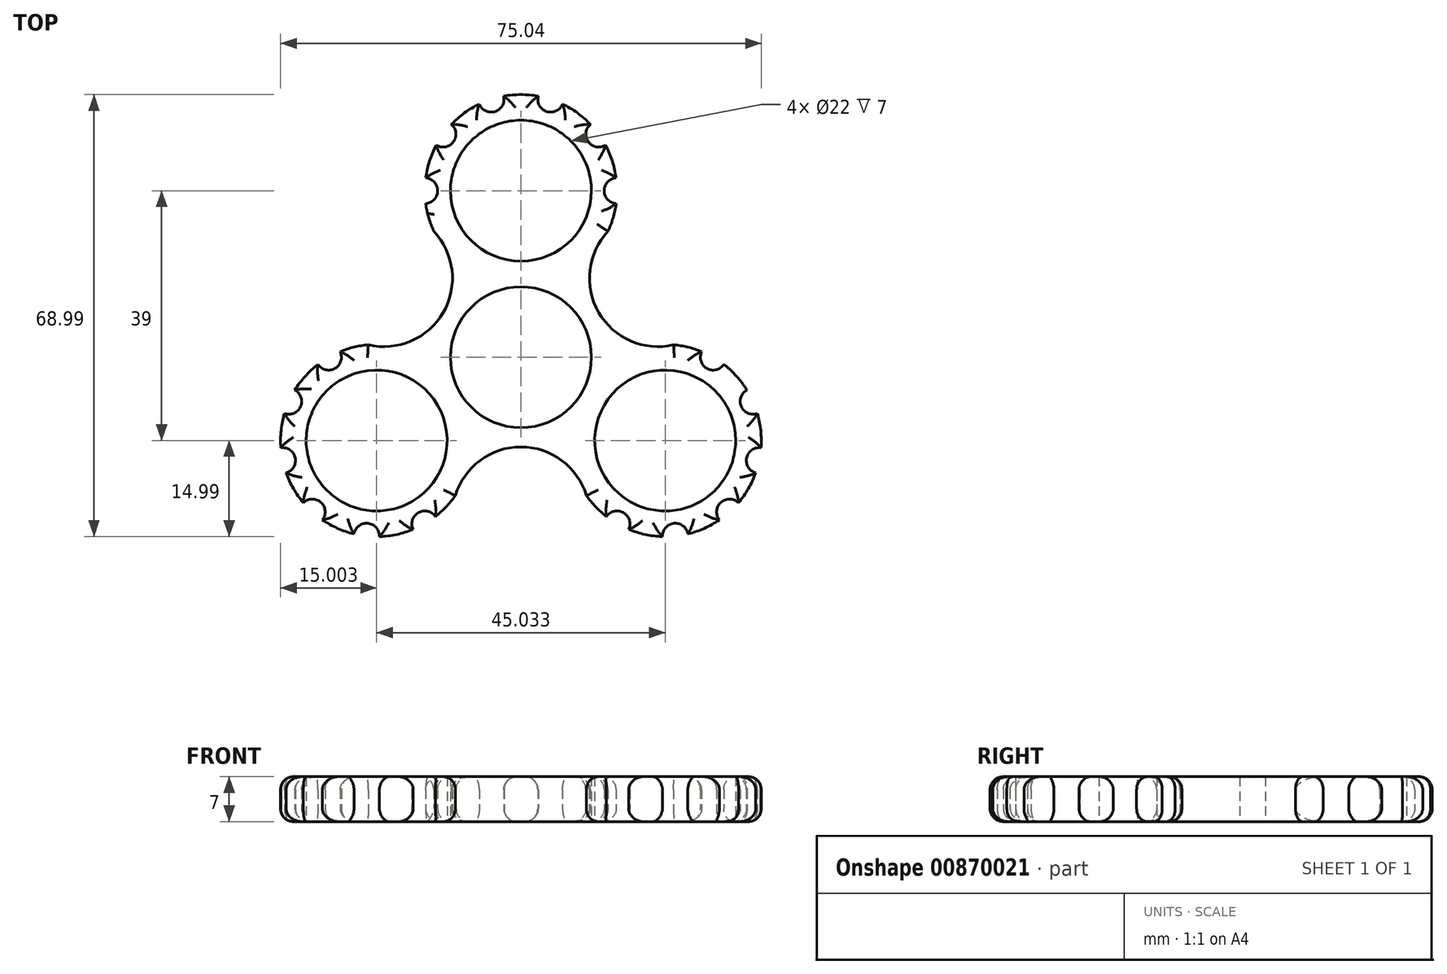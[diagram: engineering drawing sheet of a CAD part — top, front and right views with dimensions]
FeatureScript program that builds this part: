
annotation { "Feature Type Name" : "Feature", "Feature Type Description" : "" }
export const myFeature = defineFeature(function(context is Context, id is Id, definition is map)
    precondition{}
    {
        {
            var Q0;
            Q0=qCreatedBy(makeId("Top.planeOp"),FACE);
            var sketch = newSketch(context, id + "F0", { "sketchPlane" : qUnion([Q0])});
            skCircle(sketch, "E0", {"center": v(0, 0) * mm, "radius": 11 * mm});
            skCircle(sketch, "E1.0", {"center": v(0, 0) * mm, "radius": 14 * mm});
            skLineSegment(sketch, "E2", {"start": v(0, 0) * mm, "end": v(0, 26) * mm});
            skCircle(sketch, "E3", {"center": v(0, 26) * mm, "radius": 11 * mm});
            skCircle(sketch, "E4.0", {"center": v(0, 26) * mm, "radius": 15 * mm});
            skCircle(sketch, "E5", {"center": v(-15, 26) * mm, "radius": 2 * mm});
            skCircle(sketch, "E6.1.0", {"center": v(-12.14, 34.82) * mm, "radius": 2 * mm});
            skCircle(sketch, "E6.2.0", {"center": v(-4.64, 40.27) * mm, "radius": 2 * mm});
            skLineSegment(sketch, "E6.anchor1", {"start": v(0, 26) * mm, "end": v(-15, 26) * mm, "construction": true});
            skLineSegment(sketch, "E6.anchor2", {"start": v(0, 26) * mm, "end": v(15, 26) * mm, "construction": true});
            skCircle(sketch, "E7.1.3.0", {"center": v(4.64, 40.27) * mm, "radius": 2 * mm});
            skCircle(sketch, "E7.1.4.0", {"center": v(12.14, 34.82) * mm, "radius": 2 * mm});
            skPoint(sketch, "E8", {"position": v(-14.87, 24) * mm});
            skLineSegment(sketch, "E9", {"start": v(0, 0) * mm, "end": v(12.12, 7) * mm});
            skPoint(sketch, "E10.MirrorP", {"position": v(14.87, 24) * mm});
            skCircle(sketch, "E11.1.5.0", {"center": v(15, 26) * mm, "radius": 2 * mm});
            skLineSegment(sketch, "E12", {"start": v(0, 26) * mm, "end": v(13.6, 19.66) * mm});
            skCircle(sketch, "E13.1.0", {"center": v(-22.52, -13) * mm, "radius": 15 * mm});
            skCircle(sketch, "E13.1.1", {"center": v(-22.52, -13) * mm, "radius": 11 * mm});
            skCircle(sketch, "E13.1.2", {"center": v(-15.02, -26) * mm, "radius": 2 * mm});
            skCircle(sketch, "E13.1.3", {"center": v(-24.08, -27.92) * mm, "radius": 2 * mm});
            skCircle(sketch, "E13.1.4", {"center": v(-32.55, -24.15) * mm, "radius": 2 * mm});
            skCircle(sketch, "E13.1.5", {"center": v(-37.19, -16.12) * mm, "radius": 2 * mm});
            skCircle(sketch, "E13.1.6", {"center": v(-36.22, -6.9) * mm, "radius": 2 * mm});
            skCircle(sketch, "E13.1.7", {"center": v(-30.02, 0) * mm, "radius": 2 * mm});
            skCircle(sketch, "E13.2.0", {"center": v(22.52, -13) * mm, "radius": 15 * mm});
            skCircle(sketch, "E13.2.1", {"center": v(22.52, -13) * mm, "radius": 11 * mm});
            skCircle(sketch, "E13.2.2", {"center": v(30.02, 0) * mm, "radius": 2 * mm});
            skCircle(sketch, "E13.2.3", {"center": v(36.22, -6.9) * mm, "radius": 2 * mm});
            skCircle(sketch, "E13.2.4", {"center": v(37.19, -16.12) * mm, "radius": 2 * mm});
            skCircle(sketch, "E13.2.5", {"center": v(32.55, -24.15) * mm, "radius": 2 * mm});
            skCircle(sketch, "E13.2.6", {"center": v(24.08, -27.92) * mm, "radius": 2 * mm});
            skCircle(sketch, "E13.2.7", {"center": v(15.02, -26) * mm, "radius": 2 * mm});
            skLineSegment(sketch, "E14.MirrorCS", {"start": v(22.52, -13) * mm, "end": v(23.82, 1.94) * mm});
            skArc(sketch, "E15", {"start": v(13.6, 19.66) * mm, "mid": v(12.12, 7) * mm, "end": v(23.82, 1.94) * mm});
            skArc(sketch, "E16.1.0", {"start": v(-23.82, 1.94) * mm, "mid": v(-12.12, 7) * mm, "end": v(-13.6, 19.66) * mm});
            skArc(sketch, "E16.2.0", {"start": v(10.23, -21.6) * mm, "mid": v(0, -14) * mm, "end": v(-10.23, -21.6) * mm});
            skSolve(sketch);
        }
        {
            var Q0;
            {var subQ3=sQuery(id+"F0.wireOp",EDGE,"E1.0");var subQ18=sQuery(id+"F0.wireOp",EDGE,"E2");var subQ19=makeQuery(id+"F0.imprint","INTERSECT",VERTEX,{"derivedFrom":[subQ3,subQ18]});Q0=makeQuery(id+"F0.imprint","IMPRINT",FACE,{"disambiguationData":[TD([[makeQuery(id+"F0.imprint","IMPRINT",EDGE,{"disambiguationData":[TD([[subQ19,-1.0]])],"derivedFrom":subQ3}),-1.0]])]});}
            var Q1;
            {var subQ5=sQuery(id+"F0.wireOp",EDGE,"E1.0");var subQ7=sQuery(id+"F0.wireOp",EDGE,"E4.0");var subQ8=makeQuery(id+"F0.imprint","INTERSECT",VERTEX,{"disambiguationData":[OD(0.0)],"derivedFrom":[subQ5,subQ7]});Q1=makeQuery(id+"F0.imprint","IMPRINT",FACE,{"disambiguationData":[TD([[makeQuery(id+"F0.imprint","IMPRINT",EDGE,{"disambiguationData":[TD([[subQ8,-1.0]])],"derivedFrom":subQ5}),-1.0]])]});}
            var Q2;
            {var subQ0=sQuery(id+"F0.wireOp",EDGE,"E4.0");var subQ1=sQuery(id+"F0.wireOp",EDGE,"E1.0");var subQ2=makeQuery(id+"F0.imprint","INTERSECT",VERTEX,{"disambiguationData":[OD(0.0)],"derivedFrom":[subQ1,subQ0]});Q2=makeQuery(id+"F0.imprint","IMPRINT",FACE,{"disambiguationData":[TD([[makeQuery(id+"F0.imprint","IMPRINT",EDGE,{"disambiguationData":[TD([[subQ2,-1.0]])],"derivedFrom":subQ1}),1.0]])]});}
            var Q3;
            {var subQ0=sQuery(id+"F0.wireOp",EDGE,"E2");var subQ1=sQuery(id+"F0.wireOp",EDGE,"E1.0");var subQ2=makeQuery(id+"F0.imprint","INTERSECT",VERTEX,{"derivedFrom":[subQ1,subQ0]});Q3=makeQuery(id+"F0.imprint","IMPRINT",FACE,{"disambiguationData":[TD([[makeQuery(id+"F0.imprint","IMPRINT",EDGE,{"disambiguationData":[TD([[subQ2,-1.0]])],"derivedFrom":subQ1}),1.0]])]});}
            var Q4;
            {var subQ0=sQuery(id+"F0.wireOp",EDGE,"E16.1.0");var subQ1=sQuery(id+"F0.wireOp",EDGE,"E1.0");var subQ2=makeQuery(id+"F0.imprint","INTERSECT",VERTEX,{"derivedFrom":[subQ1,subQ0]});Q4=makeQuery(id+"F0.imprint","IMPRINT",FACE,{"disambiguationData":[TD([[makeQuery(id+"F0.imprint","IMPRINT",EDGE,{"disambiguationData":[TD([[subQ2,1.0]])],"derivedFrom":subQ1}),-1.0]])]});}
            var Q5;
            {var subQ1=sQuery(id+"F0.wireOp",EDGE,"E1.0");var subQ5=makeQuery(id+"F0.imprint","INTERSECT",VERTEX,{"derivedFrom":[subQ1,sQuery(id+"F0.wireOp",EDGE,"E16.1.0")]});Q5=makeQuery(id+"F0.imprint","IMPRINT",FACE,{"disambiguationData":[TD([[makeQuery(id+"F0.imprint","IMPRINT",EDGE,{"disambiguationData":[TD([[subQ5,1.0]])],"derivedFrom":subQ1}),1.0]])]});}
            var Q6;
            {var subQ0=sQuery(id+"F0.wireOp",EDGE,"E16.1.0");var subQ1=sQuery(id+"F0.wireOp",EDGE,"E1.0");var subQ2=makeQuery(id+"F0.imprint","INTERSECT",VERTEX,{"derivedFrom":[subQ1,subQ0]});Q6=makeQuery(id+"F0.imprint","IMPRINT",FACE,{"disambiguationData":[TD([[makeQuery(id+"F0.imprint","IMPRINT",EDGE,{"disambiguationData":[TD([[subQ2,-1.0]])],"derivedFrom":subQ1}),-1.0]])]});}
            var Q7;
            Q7=makeQuery(id+"F0.imprint","IMPRINT",FACE,{"disambiguationData":[TD([[makeQuery(id+"F0.imprint","IMPRINT",EDGE,{"derivedFrom":sQuery(id+"F0.wireOp",EDGE,"E13.1.1")}),-1.0]])]});
            var Q8;
            {var subQ0=sQuery(id+"F0.wireOp",EDGE,"E13.1.0");var subQ1=sQuery(id+"F0.wireOp",EDGE,"E1.0");var subQ2=makeQuery(id+"F0.imprint","INTERSECT",VERTEX,{"disambiguationData":[OD(0.0)],"derivedFrom":[subQ1,subQ0]});Q8=makeQuery(id+"F0.imprint","IMPRINT",FACE,{"disambiguationData":[TD([[makeQuery(id+"F0.imprint","IMPRINT",EDGE,{"disambiguationData":[TD([[subQ2,-1.0]])],"derivedFrom":subQ1}),1.0]])]});}
            var Q9;
            {var subQ0=sQuery(id+"F0.wireOp",EDGE,"E13.1.0");var subQ1=sQuery(id+"F0.wireOp",EDGE,"E0");var subQ2=makeQuery(id+"F0.imprint","INTERSECT",VERTEX,{"derivedFrom":[subQ1,subQ0]});Q9=makeQuery(id+"F0.imprint","IMPRINT",FACE,{"disambiguationData":[TD([[makeQuery(id+"F0.imprint","IMPRINT",EDGE,{"disambiguationData":[TD([[subQ2,-1.0]])],"derivedFrom":subQ1}),-1.0]])]});}
            var Q10;
            {var subQ0=sQuery(id+"F0.wireOp",EDGE,"E16.2.0");var subQ1=sQuery(id+"F0.wireOp",EDGE,"E1.0");var subQ2=makeQuery(id+"F0.imprint","INTERSECT",VERTEX,{"derivedFrom":[subQ1,subQ0]});Q10=makeQuery(id+"F0.imprint","IMPRINT",FACE,{"disambiguationData":[TD([[makeQuery(id+"F0.imprint","IMPRINT",EDGE,{"disambiguationData":[TD([[subQ2,1.0]])],"derivedFrom":subQ1}),-1.0]])]});}
            var Q11;
            {var subQ0=sQuery(id+"F0.wireOp",EDGE,"E16.2.0");var subQ1=sQuery(id+"F0.wireOp",EDGE,"E1.0");var subQ2=makeQuery(id+"F0.imprint","INTERSECT",VERTEX,{"derivedFrom":[subQ1,subQ0]});Q11=makeQuery(id+"F0.imprint","IMPRINT",FACE,{"disambiguationData":[TD([[makeQuery(id+"F0.imprint","IMPRINT",EDGE,{"disambiguationData":[TD([[subQ2,-1.0]])],"derivedFrom":subQ1}),-1.0]])]});}
            var Q12;
            Q12=makeQuery(id+"F0.imprint","IMPRINT",FACE,{"disambiguationData":[TD([[makeQuery(id+"F0.imprint","IMPRINT",EDGE,{"derivedFrom":sQuery(id+"F0.wireOp",EDGE,"E13.2.1")}),-1.0]])]});
            var Q13;
            {var subQ0=sQuery(id+"F0.wireOp",EDGE,"E13.2.0");var subQ1=sQuery(id+"F0.wireOp",EDGE,"E1.0");var subQ2=makeQuery(id+"F0.imprint","INTERSECT",VERTEX,{"disambiguationData":[OD(0.0)],"derivedFrom":[subQ1,subQ0]});Q13=makeQuery(id+"F0.imprint","IMPRINT",FACE,{"disambiguationData":[TD([[makeQuery(id+"F0.imprint","IMPRINT",EDGE,{"disambiguationData":[TD([[subQ2,-1.0]])],"derivedFrom":subQ1}),1.0]])]});}
            var Q14;
            {var subQ0=sQuery(id+"F0.wireOp",EDGE,"E15");var subQ3=sQuery(id+"F0.wireOp",EDGE,"E13.2.0");var subQ5=makeQuery(id+"F0.imprint","INTERSECT",VERTEX,{"disambiguationData":[OD(1.0)],"derivedFrom":[subQ3,subQ0]});Q14=makeQuery(id+"F0.imprint","IMPRINT",FACE,{"disambiguationData":[TD([[makeQuery(id+"F0.imprint","IMPRINT",EDGE,{"disambiguationData":[TD([[subQ5,-1.0]])],"derivedFrom":subQ3}),-1.0]])]});}
            var Q15;
            {var subQ0=sQuery(id+"F0.wireOp",EDGE,"E9");var subQ1=sQuery(id+"F0.wireOp",EDGE,"E0");var subQ2=makeQuery(id+"F0.imprint","INTERSECT",VERTEX,{"derivedFrom":[subQ1,subQ0]});Q15=makeQuery(id+"F0.imprint","IMPRINT",FACE,{"disambiguationData":[TD([[makeQuery(id+"F0.imprint","IMPRINT",EDGE,{"disambiguationData":[TD([[subQ2,1.0]])],"derivedFrom":subQ1}),-1.0]])]});}
            var Q16;
            {var subQ0=sQuery(id+"F0.wireOp",EDGE,"E15");var subQ3=sQuery(id+"F0.wireOp",EDGE,"E4.0");var subQ5=makeQuery(id+"F0.imprint","INTERSECT",VERTEX,{"derivedFrom":[subQ3,subQ0]});Q16=makeQuery(id+"F0.imprint","IMPRINT",FACE,{"disambiguationData":[TD([[makeQuery(id+"F0.imprint","IMPRINT",EDGE,{"disambiguationData":[TD([[subQ5,1.0]])],"derivedFrom":subQ3}),-1.0]])]});}
            var Q17;
            {var subQ0=sQuery(id+"F0.wireOp",EDGE,"E9");var subQ1=sQuery(id+"F0.wireOp",EDGE,"E0");var subQ2=makeQuery(id+"F0.imprint","INTERSECT",VERTEX,{"derivedFrom":[subQ1,subQ0]});Q17=makeQuery(id+"F0.imprint","IMPRINT",FACE,{"disambiguationData":[TD([[makeQuery(id+"F0.imprint","IMPRINT",EDGE,{"disambiguationData":[TD([[subQ2,-1.0]])],"derivedFrom":subQ1}),-1.0]])]});}
            extrude(context, id + "F1", {"entities" : qUnion([Q0, Q1, Q2, Q3, Q4, Q5, Q6, Q7, Q8, Q9, Q10, Q11, Q12, Q13, Q14, Q15, Q16, Q17]), "depth" : 7 * mm, "offsetDistance" : 25 * mm});
        }
        {
            var Q0;
            Q0=makeQuery(id+"F1.opExtrude","CAP_EDGE",EDGE,{"disambiguationData":[OSD([sQuery(id+"F0.wireOp",EDGE,"E15")])],"isStart":false});
            var Q1;
            {var subQ0=sQuery(id+"F0.wireOp",EDGE,"E13.2.0");Q1=makeQuery(id+"F1.opExtrude","CAP_EDGE",EDGE,{"disambiguationData":[OSD([subQ0]),TDD([makeQuery(id+"F0.imprint","IMPRINT",EDGE,{"disambiguationData":[TD([[makeQuery(id+"F0.imprint","INTERSECT",VERTEX,{"disambiguationData":[OD(0.0)],"derivedFrom":[subQ0,sQuery(id+"F0.wireOp",EDGE,"E15")]}),1.0]])],"derivedFrom":subQ0})])],"isStart":false});}
            var Q2;
            Q2=makeQuery(id+"F1.opExtrude","CAP_EDGE",EDGE,{"disambiguationData":[OSD([sQuery(id+"F0.wireOp",EDGE,"E13.2.2")])],"isStart":false});
            var Q3;
            {var subQ0=sQuery(id+"F0.wireOp",EDGE,"E13.2.0");Q3=makeQuery(id+"F1.opExtrude","CAP_EDGE",EDGE,{"disambiguationData":[OSD([subQ0]),TDD([makeQuery(id+"F0.imprint","IMPRINT",EDGE,{"disambiguationData":[TD([[makeQuery(id+"F0.imprint","INTERSECT",VERTEX,{"disambiguationData":[OD(1.0)],"derivedFrom":[subQ0,sQuery(id+"F0.wireOp",EDGE,"E13.2.3")]}),-1.0]])],"derivedFrom":subQ0})])],"isStart":false});}
            var Q4;
            Q4=makeQuery(id+"F1.opExtrude","CAP_EDGE",EDGE,{"disambiguationData":[OSD([sQuery(id+"F0.wireOp",EDGE,"E13.2.3")])],"isStart":false});
            var Q5;
            {var subQ0=sQuery(id+"F0.wireOp",EDGE,"E13.2.0");Q5=makeQuery(id+"F1.opExtrude","CAP_EDGE",EDGE,{"disambiguationData":[OSD([subQ0]),TDD([makeQuery(id+"F0.imprint","IMPRINT",EDGE,{"disambiguationData":[TD([[makeQuery(id+"F0.imprint","INTERSECT",VERTEX,{"disambiguationData":[OD(1.0)],"derivedFrom":[subQ0,sQuery(id+"F0.wireOp",EDGE,"E13.2.4")]}),-1.0]])],"derivedFrom":subQ0})])],"isStart":false});}
            var Q6;
            Q6=makeQuery(id+"F1.opExtrude","CAP_EDGE",EDGE,{"disambiguationData":[OSD([sQuery(id+"F0.wireOp",EDGE,"E13.2.4")])],"isStart":false});
            var Q7;
            {var subQ0=sQuery(id+"F0.wireOp",EDGE,"E13.2.0");Q7=makeQuery(id+"F1.opExtrude","CAP_EDGE",EDGE,{"disambiguationData":[OSD([subQ0]),TDD([makeQuery(id+"F0.imprint","IMPRINT",EDGE,{"disambiguationData":[TD([[makeQuery(id+"F0.imprint","INTERSECT",VERTEX,{"disambiguationData":[OD(1.0)],"derivedFrom":[subQ0,sQuery(id+"F0.wireOp",EDGE,"E13.2.5")]}),-1.0]])],"derivedFrom":subQ0})])],"isStart":false});}
            var Q8;
            Q8=makeQuery(id+"F1.opExtrude","CAP_EDGE",EDGE,{"disambiguationData":[OSD([sQuery(id+"F0.wireOp",EDGE,"E13.2.5")])],"isStart":false});
            var Q9;
            {var subQ0=sQuery(id+"F0.wireOp",EDGE,"E13.2.0");Q9=makeQuery(id+"F1.opExtrude","CAP_EDGE",EDGE,{"disambiguationData":[OSD([subQ0]),TDD([makeQuery(id+"F0.imprint","IMPRINT",EDGE,{"disambiguationData":[TD([[makeQuery(id+"F0.imprint","INTERSECT",VERTEX,{"disambiguationData":[OD(1.0)],"derivedFrom":[subQ0,sQuery(id+"F0.wireOp",EDGE,"E13.2.6")]}),-1.0]])],"derivedFrom":subQ0})])],"isStart":false});}
            var Q10;
            Q10=makeQuery(id+"F1.opExtrude","CAP_EDGE",EDGE,{"disambiguationData":[OSD([sQuery(id+"F0.wireOp",EDGE,"E13.2.6")])],"isStart":false});
            var Q11;
            {var subQ0=sQuery(id+"F0.wireOp",EDGE,"E13.2.0");Q11=makeQuery(id+"F1.opExtrude","CAP_EDGE",EDGE,{"disambiguationData":[OSD([subQ0]),TDD([makeQuery(id+"F0.imprint","IMPRINT",EDGE,{"disambiguationData":[TD([[makeQuery(id+"F0.imprint","INTERSECT",VERTEX,{"disambiguationData":[OD(0.0)],"derivedFrom":[subQ0,sQuery(id+"F0.wireOp",EDGE,"E13.2.6")]}),1.0]])],"derivedFrom":subQ0})])],"isStart":false});}
            var Q12;
            Q12=makeQuery(id+"F1.opExtrude","CAP_EDGE",EDGE,{"disambiguationData":[OSD([sQuery(id+"F0.wireOp",EDGE,"E13.2.7")])],"isStart":false});
            var Q13;
            {var subQ0=sQuery(id+"F0.wireOp",EDGE,"E13.2.0");Q13=makeQuery(id+"F1.opExtrude","CAP_EDGE",EDGE,{"disambiguationData":[OSD([subQ0]),TDD([makeQuery(id+"F0.imprint","IMPRINT",EDGE,{"disambiguationData":[TD([[makeQuery(id+"F0.imprint","INTERSECT",VERTEX,{"disambiguationData":[OD(0.0)],"derivedFrom":[subQ0,sQuery(id+"F0.wireOp",EDGE,"E16.2.0")]}),-1.0]])],"derivedFrom":subQ0})])],"isStart":false});}
            var Q14;
            Q14=makeQuery(id+"F1.opExtrude","CAP_EDGE",EDGE,{"disambiguationData":[OSD([sQuery(id+"F0.wireOp",EDGE,"E16.2.0")])],"isStart":false});
            var Q15;
            {var subQ0=sQuery(id+"F0.wireOp",EDGE,"E13.1.0");Q15=makeQuery(id+"F1.opExtrude","CAP_EDGE",EDGE,{"disambiguationData":[OSD([subQ0]),TDD([makeQuery(id+"F0.imprint","IMPRINT",EDGE,{"disambiguationData":[TD([[makeQuery(id+"F0.imprint","INTERSECT",VERTEX,{"disambiguationData":[OD(0.0)],"derivedFrom":[subQ0,sQuery(id+"F0.wireOp",EDGE,"E16.2.0")]}),1.0]])],"derivedFrom":subQ0})])],"isStart":false});}
            var Q16;
            Q16=makeQuery(id+"F1.opExtrude","CAP_EDGE",EDGE,{"disambiguationData":[OSD([sQuery(id+"F0.wireOp",EDGE,"E13.1.2")])],"isStart":false});
            var Q17;
            {var subQ0=sQuery(id+"F0.wireOp",EDGE,"E13.1.0");Q17=makeQuery(id+"F1.opExtrude","CAP_EDGE",EDGE,{"disambiguationData":[OSD([subQ0]),TDD([makeQuery(id+"F0.imprint","IMPRINT",EDGE,{"disambiguationData":[TD([[makeQuery(id+"F0.imprint","INTERSECT",VERTEX,{"disambiguationData":[OD(1.0)],"derivedFrom":[subQ0,sQuery(id+"F0.wireOp",EDGE,"E13.1.3")]}),-1.0]])],"derivedFrom":subQ0})])],"isStart":false});}
            var Q18;
            Q18=makeQuery(id+"F1.opExtrude","CAP_EDGE",EDGE,{"disambiguationData":[OSD([sQuery(id+"F0.wireOp",EDGE,"E13.1.3")])],"isStart":false});
            var Q19;
            {var subQ0=sQuery(id+"F0.wireOp",EDGE,"E13.1.0");Q19=makeQuery(id+"F1.opExtrude","CAP_EDGE",EDGE,{"disambiguationData":[OSD([subQ0]),TDD([makeQuery(id+"F0.imprint","IMPRINT",EDGE,{"disambiguationData":[TD([[makeQuery(id+"F0.imprint","INTERSECT",VERTEX,{"disambiguationData":[OD(1.0)],"derivedFrom":[subQ0,sQuery(id+"F0.wireOp",EDGE,"E13.1.4")]}),-1.0]])],"derivedFrom":subQ0})])],"isStart":false});}
            var Q20;
            Q20=makeQuery(id+"F1.opExtrude","CAP_EDGE",EDGE,{"disambiguationData":[OSD([sQuery(id+"F0.wireOp",EDGE,"E13.1.4")])],"isStart":false});
            var Q21;
            {var subQ0=sQuery(id+"F0.wireOp",EDGE,"E13.1.0");Q21=makeQuery(id+"F1.opExtrude","CAP_EDGE",EDGE,{"disambiguationData":[OSD([subQ0]),TDD([makeQuery(id+"F0.imprint","IMPRINT",EDGE,{"disambiguationData":[TD([[makeQuery(id+"F0.imprint","INTERSECT",VERTEX,{"disambiguationData":[OD(1.0)],"derivedFrom":[subQ0,sQuery(id+"F0.wireOp",EDGE,"E13.1.5")]}),-1.0]])],"derivedFrom":subQ0})])],"isStart":false});}
            var Q22;
            Q22=makeQuery(id+"F1.opExtrude","CAP_EDGE",EDGE,{"disambiguationData":[OSD([sQuery(id+"F0.wireOp",EDGE,"E13.1.5")])],"isStart":false});
            var Q23;
            {var subQ0=sQuery(id+"F0.wireOp",EDGE,"E13.1.0");Q23=makeQuery(id+"F1.opExtrude","CAP_EDGE",EDGE,{"disambiguationData":[OSD([subQ0]),TDD([makeQuery(id+"F0.imprint","IMPRINT",EDGE,{"disambiguationData":[TD([[makeQuery(id+"F0.imprint","INTERSECT",VERTEX,{"disambiguationData":[OD(1.0)],"derivedFrom":[subQ0,sQuery(id+"F0.wireOp",EDGE,"E13.1.6")]}),-1.0]])],"derivedFrom":subQ0})])],"isStart":false});}
            var Q24;
            Q24=makeQuery(id+"F1.opExtrude","CAP_EDGE",EDGE,{"disambiguationData":[OSD([sQuery(id+"F0.wireOp",EDGE,"E13.1.6")])],"isStart":false});
            var Q25;
            {var subQ0=sQuery(id+"F0.wireOp",EDGE,"E13.1.0");Q25=makeQuery(id+"F1.opExtrude","CAP_EDGE",EDGE,{"disambiguationData":[OSD([subQ0]),TDD([makeQuery(id+"F0.imprint","IMPRINT",EDGE,{"disambiguationData":[TD([[makeQuery(id+"F0.imprint","INTERSECT",VERTEX,{"disambiguationData":[OD(0.0)],"derivedFrom":[subQ0,sQuery(id+"F0.wireOp",EDGE,"E13.1.6")]}),1.0]])],"derivedFrom":subQ0})])],"isStart":false});}
            var Q26;
            Q26=makeQuery(id+"F1.opExtrude","CAP_EDGE",EDGE,{"disambiguationData":[OSD([sQuery(id+"F0.wireOp",EDGE,"E13.1.7")])],"isStart":false});
            var Q27;
            {var subQ0=sQuery(id+"F0.wireOp",EDGE,"E13.1.0");Q27=makeQuery(id+"F1.opExtrude","CAP_EDGE",EDGE,{"disambiguationData":[OSD([subQ0]),TDD([makeQuery(id+"F0.imprint","IMPRINT",EDGE,{"disambiguationData":[TD([[makeQuery(id+"F0.imprint","INTERSECT",VERTEX,{"disambiguationData":[OD(0.0)],"derivedFrom":[subQ0,sQuery(id+"F0.wireOp",EDGE,"E16.1.0")]}),-1.0]])],"derivedFrom":subQ0})])],"isStart":false});}
            var Q28;
            Q28=makeQuery(id+"F1.opExtrude","CAP_EDGE",EDGE,{"disambiguationData":[OSD([sQuery(id+"F0.wireOp",EDGE,"E16.1.0")])],"isStart":false});
            var Q29;
            Q29=makeQuery(id+"F1.opExtrude","CAP_EDGE",EDGE,{"disambiguationData":[OSD([sQuery(id+"F0.wireOp",EDGE,"E5")])],"isStart":false});
            var Q30;
            {var subQ0=sQuery(id+"F0.wireOp",EDGE,"E4.0");Q30=makeQuery(id+"F1.opExtrude","CAP_EDGE",EDGE,{"disambiguationData":[OSD([subQ0]),TDD([makeQuery(id+"F0.imprint","IMPRINT",EDGE,{"disambiguationData":[TD([[makeQuery(id+"F0.imprint","INTERSECT",VERTEX,{"disambiguationData":[OD(0.0)],"derivedFrom":[subQ0,sQuery(id+"F0.wireOp",EDGE,"E16.1.0")]}),1.0]])],"derivedFrom":subQ0})])],"isStart":false});}
            var Q31;
            {var subQ0=sQuery(id+"F0.wireOp",EDGE,"E4.0");Q31=makeQuery(id+"F1.opExtrude","CAP_EDGE",EDGE,{"disambiguationData":[OSD([subQ0]),TDD([makeQuery(id+"F0.imprint","IMPRINT",EDGE,{"disambiguationData":[TD([[makeQuery(id+"F0.imprint","INTERSECT",VERTEX,{"disambiguationData":[OD(1.0)],"derivedFrom":[subQ0,sQuery(id+"F0.wireOp",EDGE,"E6.1.0")]}),-1.0]])],"derivedFrom":subQ0})])],"isStart":false});}
            var Q32;
            Q32=makeQuery(id+"F1.opExtrude","CAP_EDGE",EDGE,{"disambiguationData":[OSD([sQuery(id+"F0.wireOp",EDGE,"E6.1.0")])],"isStart":false});
            var Q33;
            {var subQ0=sQuery(id+"F0.wireOp",EDGE,"E4.0");Q33=makeQuery(id+"F1.opExtrude","CAP_EDGE",EDGE,{"disambiguationData":[OSD([subQ0]),TDD([makeQuery(id+"F0.imprint","IMPRINT",EDGE,{"disambiguationData":[TD([[makeQuery(id+"F0.imprint","INTERSECT",VERTEX,{"disambiguationData":[OD(1.0)],"derivedFrom":[subQ0,sQuery(id+"F0.wireOp",EDGE,"E6.2.0")]}),-1.0]])],"derivedFrom":subQ0})])],"isStart":false});}
            var Q34;
            Q34=makeQuery(id+"F1.opExtrude","CAP_EDGE",EDGE,{"disambiguationData":[OSD([sQuery(id+"F0.wireOp",EDGE,"E6.2.0")])],"isStart":false});
            var Q35;
            Q35=makeQuery(id+"F1.opExtrude","CAP_EDGE",EDGE,{"disambiguationData":[OSD([sQuery(id+"F0.wireOp",EDGE,"E7.1.3.0")])],"isStart":false});
            var Q36;
            {var subQ0=sQuery(id+"F0.wireOp",EDGE,"E4.0");Q36=makeQuery(id+"F1.opExtrude","CAP_EDGE",EDGE,{"disambiguationData":[OSD([subQ0]),TDD([makeQuery(id+"F0.imprint","IMPRINT",EDGE,{"disambiguationData":[TD([[makeQuery(id+"F0.imprint","INTERSECT",VERTEX,{"disambiguationData":[OD(1.0)],"derivedFrom":[subQ0,sQuery(id+"F0.wireOp",EDGE,"E7.1.3.0")]}),-1.0]])],"derivedFrom":subQ0})])],"isStart":false});}
            var Q37;
            {var subQ0=sQuery(id+"F0.wireOp",EDGE,"E4.0");Q37=makeQuery(id+"F1.opExtrude","CAP_EDGE",EDGE,{"disambiguationData":[OSD([subQ0]),TDD([makeQuery(id+"F0.imprint","IMPRINT",EDGE,{"disambiguationData":[TD([[makeQuery(id+"F0.imprint","INTERSECT",VERTEX,{"disambiguationData":[OD(1.0)],"derivedFrom":[subQ0,sQuery(id+"F0.wireOp",EDGE,"E7.1.4.0")]}),-1.0]])],"derivedFrom":subQ0})])],"isStart":false});}
            var Q38;
            Q38=makeQuery(id+"F1.opExtrude","CAP_EDGE",EDGE,{"disambiguationData":[OSD([sQuery(id+"F0.wireOp",EDGE,"E7.1.4.0")])],"isStart":false});
            var Q39;
            {var subQ0=sQuery(id+"F0.wireOp",EDGE,"E4.0");Q39=makeQuery(id+"F1.opExtrude","CAP_EDGE",EDGE,{"disambiguationData":[OSD([subQ0]),TDD([makeQuery(id+"F0.imprint","IMPRINT",EDGE,{"disambiguationData":[TD([[makeQuery(id+"F0.imprint","INTERSECT",VERTEX,{"disambiguationData":[OD(0.0)],"derivedFrom":[subQ0,sQuery(id+"F0.wireOp",EDGE,"E7.1.4.0")]}),1.0]])],"derivedFrom":subQ0})])],"isStart":false});}
            var Q40;
            Q40=makeQuery(id+"F1.opExtrude","CAP_EDGE",EDGE,{"disambiguationData":[OSD([sQuery(id+"F0.wireOp",EDGE,"E11.1.5.0")])],"isStart":false});
            var Q41;
            {var subQ0=sQuery(id+"F0.wireOp",EDGE,"E4.0");Q41=makeQuery(id+"F1.opExtrude","CAP_EDGE",EDGE,{"disambiguationData":[OSD([subQ0]),TDD([makeQuery(id+"F0.imprint","IMPRINT",EDGE,{"disambiguationData":[TD([[makeQuery(id+"F0.imprint","INTERSECT",VERTEX,{"disambiguationData":[OD(1.0)],"derivedFrom":[subQ0,sQuery(id+"F0.wireOp",EDGE,"E11.1.5.0")]}),1.0]])],"derivedFrom":subQ0})])],"isStart":false});}
            fillet(context, id + "F2", {"entities" : qUnion([Q0, Q1, Q2, Q3, Q4, Q5, Q6, Q7, Q8, Q9, Q10, Q11, Q12, Q13, Q14, Q15, Q16, Q17, Q18, Q19, Q20, Q21, Q22, Q23, Q24, Q25, Q26, Q27, Q28, Q29, Q30, Q31, Q32, Q33, Q34, Q35, Q36, Q37, Q38, Q39, Q40, Q41]), "radius" : 2 * mm, "tangentPropagation" : true, "allowEdgeOverflow" : false});
        }
        {
            var Q0;
            Q0=makeQuery(id+"F1.opExtrude","CAP_EDGE",EDGE,{"disambiguationData":[OSD([sQuery(id+"F0.wireOp",EDGE,"E16.1.0")])],"isStart":true});
            var Q1;
            {var subQ0=sQuery(id+"F0.wireOp",EDGE,"E13.1.0");Q1=makeQuery(id+"F1.opExtrude","CAP_EDGE",EDGE,{"disambiguationData":[OSD([subQ0]),TDD([makeQuery(id+"F0.imprint","IMPRINT",EDGE,{"disambiguationData":[TD([[makeQuery(id+"F0.imprint","INTERSECT",VERTEX,{"disambiguationData":[OD(0.0)],"derivedFrom":[subQ0,sQuery(id+"F0.wireOp",EDGE,"E16.1.0")]}),-1.0]])],"derivedFrom":subQ0})])],"isStart":true});}
            var Q2;
            Q2=makeQuery(id+"F1.opExtrude","CAP_EDGE",EDGE,{"disambiguationData":[OSD([sQuery(id+"F0.wireOp",EDGE,"E13.1.7")])],"isStart":true});
            var Q3;
            {var subQ0=sQuery(id+"F0.wireOp",EDGE,"E13.1.0");Q3=makeQuery(id+"F1.opExtrude","CAP_EDGE",EDGE,{"disambiguationData":[OSD([subQ0]),TDD([makeQuery(id+"F0.imprint","IMPRINT",EDGE,{"disambiguationData":[TD([[makeQuery(id+"F0.imprint","INTERSECT",VERTEX,{"disambiguationData":[OD(0.0)],"derivedFrom":[subQ0,sQuery(id+"F0.wireOp",EDGE,"E13.1.6")]}),1.0]])],"derivedFrom":subQ0})])],"isStart":true});}
            var Q4;
            Q4=makeQuery(id+"F1.opExtrude","CAP_EDGE",EDGE,{"disambiguationData":[OSD([sQuery(id+"F0.wireOp",EDGE,"E13.1.6")])],"isStart":true});
            var Q5;
            {var subQ0=sQuery(id+"F0.wireOp",EDGE,"E13.1.0");Q5=makeQuery(id+"F1.opExtrude","CAP_EDGE",EDGE,{"disambiguationData":[OSD([subQ0]),TDD([makeQuery(id+"F0.imprint","IMPRINT",EDGE,{"disambiguationData":[TD([[makeQuery(id+"F0.imprint","INTERSECT",VERTEX,{"disambiguationData":[OD(1.0)],"derivedFrom":[subQ0,sQuery(id+"F0.wireOp",EDGE,"E13.1.6")]}),-1.0]])],"derivedFrom":subQ0})])],"isStart":true});}
            var Q6;
            Q6=makeQuery(id+"F1.opExtrude","CAP_EDGE",EDGE,{"disambiguationData":[OSD([sQuery(id+"F0.wireOp",EDGE,"E13.1.5")])],"isStart":true});
            var Q7;
            {var subQ0=sQuery(id+"F0.wireOp",EDGE,"E13.1.0");Q7=makeQuery(id+"F1.opExtrude","CAP_EDGE",EDGE,{"disambiguationData":[OSD([subQ0]),TDD([makeQuery(id+"F0.imprint","IMPRINT",EDGE,{"disambiguationData":[TD([[makeQuery(id+"F0.imprint","INTERSECT",VERTEX,{"disambiguationData":[OD(1.0)],"derivedFrom":[subQ0,sQuery(id+"F0.wireOp",EDGE,"E13.1.5")]}),-1.0]])],"derivedFrom":subQ0})])],"isStart":true});}
            var Q8;
            Q8=makeQuery(id+"F1.opExtrude","CAP_EDGE",EDGE,{"disambiguationData":[OSD([sQuery(id+"F0.wireOp",EDGE,"E13.1.4")])],"isStart":true});
            var Q9;
            {var subQ0=sQuery(id+"F0.wireOp",EDGE,"E13.1.0");Q9=makeQuery(id+"F1.opExtrude","CAP_EDGE",EDGE,{"disambiguationData":[OSD([subQ0]),TDD([makeQuery(id+"F0.imprint","IMPRINT",EDGE,{"disambiguationData":[TD([[makeQuery(id+"F0.imprint","INTERSECT",VERTEX,{"disambiguationData":[OD(1.0)],"derivedFrom":[subQ0,sQuery(id+"F0.wireOp",EDGE,"E13.1.4")]}),-1.0]])],"derivedFrom":subQ0})])],"isStart":true});}
            var Q10;
            Q10=makeQuery(id+"F1.opExtrude","CAP_EDGE",EDGE,{"disambiguationData":[OSD([sQuery(id+"F0.wireOp",EDGE,"E13.1.3")])],"isStart":true});
            var Q11;
            {var subQ0=sQuery(id+"F0.wireOp",EDGE,"E13.1.0");Q11=makeQuery(id+"F1.opExtrude","CAP_EDGE",EDGE,{"disambiguationData":[OSD([subQ0]),TDD([makeQuery(id+"F0.imprint","IMPRINT",EDGE,{"disambiguationData":[TD([[makeQuery(id+"F0.imprint","INTERSECT",VERTEX,{"disambiguationData":[OD(1.0)],"derivedFrom":[subQ0,sQuery(id+"F0.wireOp",EDGE,"E13.1.3")]}),-1.0]])],"derivedFrom":subQ0})])],"isStart":true});}
            var Q12;
            Q12=makeQuery(id+"F1.opExtrude","CAP_EDGE",EDGE,{"disambiguationData":[OSD([sQuery(id+"F0.wireOp",EDGE,"E13.1.2")])],"isStart":true});
            var Q13;
            {var subQ0=sQuery(id+"F0.wireOp",EDGE,"E13.1.0");Q13=makeQuery(id+"F1.opExtrude","CAP_EDGE",EDGE,{"disambiguationData":[OSD([subQ0]),TDD([makeQuery(id+"F0.imprint","IMPRINT",EDGE,{"disambiguationData":[TD([[makeQuery(id+"F0.imprint","INTERSECT",VERTEX,{"disambiguationData":[OD(0.0)],"derivedFrom":[subQ0,sQuery(id+"F0.wireOp",EDGE,"E16.2.0")]}),1.0]])],"derivedFrom":subQ0})])],"isStart":true});}
            var Q14;
            Q14=makeQuery(id+"F1.opExtrude","CAP_EDGE",EDGE,{"disambiguationData":[OSD([sQuery(id+"F0.wireOp",EDGE,"E16.2.0")])],"isStart":true});
            var Q15;
            {var subQ0=sQuery(id+"F0.wireOp",EDGE,"E13.2.0");Q15=makeQuery(id+"F1.opExtrude","CAP_EDGE",EDGE,{"disambiguationData":[OSD([subQ0]),TDD([makeQuery(id+"F0.imprint","IMPRINT",EDGE,{"disambiguationData":[TD([[makeQuery(id+"F0.imprint","INTERSECT",VERTEX,{"disambiguationData":[OD(0.0)],"derivedFrom":[subQ0,sQuery(id+"F0.wireOp",EDGE,"E16.2.0")]}),-1.0]])],"derivedFrom":subQ0})])],"isStart":true});}
            var Q16;
            Q16=makeQuery(id+"F1.opExtrude","CAP_EDGE",EDGE,{"disambiguationData":[OSD([sQuery(id+"F0.wireOp",EDGE,"E13.2.7")])],"isStart":true});
            var Q17;
            {var subQ0=sQuery(id+"F0.wireOp",EDGE,"E13.2.0");Q17=makeQuery(id+"F1.opExtrude","CAP_EDGE",EDGE,{"disambiguationData":[OSD([subQ0]),TDD([makeQuery(id+"F0.imprint","IMPRINT",EDGE,{"disambiguationData":[TD([[makeQuery(id+"F0.imprint","INTERSECT",VERTEX,{"disambiguationData":[OD(0.0)],"derivedFrom":[subQ0,sQuery(id+"F0.wireOp",EDGE,"E13.2.6")]}),1.0]])],"derivedFrom":subQ0})])],"isStart":true});}
            var Q18;
            Q18=makeQuery(id+"F1.opExtrude","CAP_EDGE",EDGE,{"disambiguationData":[OSD([sQuery(id+"F0.wireOp",EDGE,"E13.2.6")])],"isStart":true});
            var Q19;
            {var subQ0=sQuery(id+"F0.wireOp",EDGE,"E13.2.0");Q19=makeQuery(id+"F1.opExtrude","CAP_EDGE",EDGE,{"disambiguationData":[OSD([subQ0]),TDD([makeQuery(id+"F0.imprint","IMPRINT",EDGE,{"disambiguationData":[TD([[makeQuery(id+"F0.imprint","INTERSECT",VERTEX,{"disambiguationData":[OD(1.0)],"derivedFrom":[subQ0,sQuery(id+"F0.wireOp",EDGE,"E13.2.6")]}),-1.0]])],"derivedFrom":subQ0})])],"isStart":true});}
            var Q20;
            Q20=makeQuery(id+"F1.opExtrude","CAP_EDGE",EDGE,{"disambiguationData":[OSD([sQuery(id+"F0.wireOp",EDGE,"E13.2.4")])],"isStart":true});
            var Q21;
            {var subQ0=sQuery(id+"F0.wireOp",EDGE,"E13.2.0");Q21=makeQuery(id+"F1.opExtrude","CAP_EDGE",EDGE,{"disambiguationData":[OSD([subQ0]),TDD([makeQuery(id+"F0.imprint","IMPRINT",EDGE,{"disambiguationData":[TD([[makeQuery(id+"F0.imprint","INTERSECT",VERTEX,{"disambiguationData":[OD(1.0)],"derivedFrom":[subQ0,sQuery(id+"F0.wireOp",EDGE,"E13.2.4")]}),-1.0]])],"derivedFrom":subQ0})])],"isStart":true});}
            var Q22;
            {var subQ0=sQuery(id+"F0.wireOp",EDGE,"E13.2.0");Q22=makeQuery(id+"F1.opExtrude","CAP_EDGE",EDGE,{"disambiguationData":[OSD([subQ0]),TDD([makeQuery(id+"F0.imprint","IMPRINT",EDGE,{"disambiguationData":[TD([[makeQuery(id+"F0.imprint","INTERSECT",VERTEX,{"disambiguationData":[OD(1.0)],"derivedFrom":[subQ0,sQuery(id+"F0.wireOp",EDGE,"E13.2.5")]}),-1.0]])],"derivedFrom":subQ0})])],"isStart":true});}
            var Q23;
            Q23=makeQuery(id+"F1.opExtrude","CAP_EDGE",EDGE,{"disambiguationData":[OSD([sQuery(id+"F0.wireOp",EDGE,"E13.2.3")])],"isStart":true});
            var Q24;
            {var subQ0=sQuery(id+"F0.wireOp",EDGE,"E13.2.0");Q24=makeQuery(id+"F1.opExtrude","CAP_EDGE",EDGE,{"disambiguationData":[OSD([subQ0]),TDD([makeQuery(id+"F0.imprint","IMPRINT",EDGE,{"disambiguationData":[TD([[makeQuery(id+"F0.imprint","INTERSECT",VERTEX,{"disambiguationData":[OD(1.0)],"derivedFrom":[subQ0,sQuery(id+"F0.wireOp",EDGE,"E13.2.3")]}),-1.0]])],"derivedFrom":subQ0})])],"isStart":true});}
            var Q25;
            Q25=makeQuery(id+"F1.opExtrude","CAP_EDGE",EDGE,{"disambiguationData":[OSD([sQuery(id+"F0.wireOp",EDGE,"E13.2.2")])],"isStart":true});
            var Q26;
            {var subQ0=sQuery(id+"F0.wireOp",EDGE,"E13.2.0");Q26=makeQuery(id+"F1.opExtrude","CAP_EDGE",EDGE,{"disambiguationData":[OSD([subQ0]),TDD([makeQuery(id+"F0.imprint","IMPRINT",EDGE,{"disambiguationData":[TD([[makeQuery(id+"F0.imprint","INTERSECT",VERTEX,{"disambiguationData":[OD(0.0)],"derivedFrom":[subQ0,sQuery(id+"F0.wireOp",EDGE,"E15")]}),1.0]])],"derivedFrom":subQ0})])],"isStart":true});}
            var Q27;
            Q27=makeQuery(id+"F1.opExtrude","CAP_EDGE",EDGE,{"disambiguationData":[OSD([sQuery(id+"F0.wireOp",EDGE,"E15")])],"isStart":true});
            var Q28;
            {var subQ0=sQuery(id+"F0.wireOp",EDGE,"E4.0");Q28=makeQuery(id+"F1.opExtrude","CAP_EDGE",EDGE,{"disambiguationData":[OSD([subQ0]),TDD([makeQuery(id+"F0.imprint","IMPRINT",EDGE,{"disambiguationData":[TD([[makeQuery(id+"F0.imprint","INTERSECT",VERTEX,{"disambiguationData":[OD(1.0)],"derivedFrom":[subQ0,sQuery(id+"F0.wireOp",EDGE,"E11.1.5.0")]}),1.0]])],"derivedFrom":subQ0})])],"isStart":true});}
            var Q29;
            Q29=makeQuery(id+"F1.opExtrude","CAP_EDGE",EDGE,{"disambiguationData":[OSD([sQuery(id+"F0.wireOp",EDGE,"E11.1.5.0")])],"isStart":true});
            var Q30;
            {var subQ0=sQuery(id+"F0.wireOp",EDGE,"E4.0");Q30=makeQuery(id+"F1.opExtrude","CAP_EDGE",EDGE,{"disambiguationData":[OSD([subQ0]),TDD([makeQuery(id+"F0.imprint","IMPRINT",EDGE,{"disambiguationData":[TD([[makeQuery(id+"F0.imprint","INTERSECT",VERTEX,{"disambiguationData":[OD(0.0)],"derivedFrom":[subQ0,sQuery(id+"F0.wireOp",EDGE,"E7.1.4.0")]}),1.0]])],"derivedFrom":subQ0})])],"isStart":true});}
            var Q31;
            Q31=makeQuery(id+"F1.opExtrude","CAP_EDGE",EDGE,{"disambiguationData":[OSD([sQuery(id+"F0.wireOp",EDGE,"E7.1.4.0")])],"isStart":true});
            var Q32;
            {var subQ0=sQuery(id+"F0.wireOp",EDGE,"E4.0");Q32=makeQuery(id+"F1.opExtrude","CAP_EDGE",EDGE,{"disambiguationData":[OSD([subQ0]),TDD([makeQuery(id+"F0.imprint","IMPRINT",EDGE,{"disambiguationData":[TD([[makeQuery(id+"F0.imprint","INTERSECT",VERTEX,{"disambiguationData":[OD(1.0)],"derivedFrom":[subQ0,sQuery(id+"F0.wireOp",EDGE,"E7.1.4.0")]}),-1.0]])],"derivedFrom":subQ0})])],"isStart":true});}
            var Q33;
            Q33=makeQuery(id+"F1.opExtrude","CAP_EDGE",EDGE,{"disambiguationData":[OSD([sQuery(id+"F0.wireOp",EDGE,"E7.1.3.0")])],"isStart":true});
            var Q34;
            {var subQ0=sQuery(id+"F0.wireOp",EDGE,"E4.0");Q34=makeQuery(id+"F1.opExtrude","CAP_EDGE",EDGE,{"disambiguationData":[OSD([subQ0]),TDD([makeQuery(id+"F0.imprint","IMPRINT",EDGE,{"disambiguationData":[TD([[makeQuery(id+"F0.imprint","INTERSECT",VERTEX,{"disambiguationData":[OD(1.0)],"derivedFrom":[subQ0,sQuery(id+"F0.wireOp",EDGE,"E7.1.3.0")]}),-1.0]])],"derivedFrom":subQ0})])],"isStart":true});}
            var Q35;
            Q35=makeQuery(id+"F1.opExtrude","CAP_EDGE",EDGE,{"disambiguationData":[OSD([sQuery(id+"F0.wireOp",EDGE,"E6.2.0")])],"isStart":true});
            var Q36;
            {var subQ0=sQuery(id+"F0.wireOp",EDGE,"E4.0");Q36=makeQuery(id+"F1.opExtrude","CAP_EDGE",EDGE,{"disambiguationData":[OSD([subQ0]),TDD([makeQuery(id+"F0.imprint","IMPRINT",EDGE,{"disambiguationData":[TD([[makeQuery(id+"F0.imprint","INTERSECT",VERTEX,{"disambiguationData":[OD(1.0)],"derivedFrom":[subQ0,sQuery(id+"F0.wireOp",EDGE,"E6.2.0")]}),-1.0]])],"derivedFrom":subQ0})])],"isStart":true});}
            var Q37;
            Q37=makeQuery(id+"F1.opExtrude","CAP_EDGE",EDGE,{"disambiguationData":[OSD([sQuery(id+"F0.wireOp",EDGE,"E6.1.0")])],"isStart":true});
            var Q38;
            {var subQ0=sQuery(id+"F0.wireOp",EDGE,"E4.0");Q38=makeQuery(id+"F1.opExtrude","CAP_EDGE",EDGE,{"disambiguationData":[OSD([subQ0]),TDD([makeQuery(id+"F0.imprint","IMPRINT",EDGE,{"disambiguationData":[TD([[makeQuery(id+"F0.imprint","INTERSECT",VERTEX,{"disambiguationData":[OD(1.0)],"derivedFrom":[subQ0,sQuery(id+"F0.wireOp",EDGE,"E6.1.0")]}),-1.0]])],"derivedFrom":subQ0})])],"isStart":true});}
            var Q39;
            Q39=makeQuery(id+"F1.opExtrude","CAP_EDGE",EDGE,{"disambiguationData":[OSD([sQuery(id+"F0.wireOp",EDGE,"E5")])],"isStart":true});
            var Q40;
            {var subQ0=sQuery(id+"F0.wireOp",EDGE,"E4.0");Q40=makeQuery(id+"F1.opExtrude","CAP_EDGE",EDGE,{"disambiguationData":[OSD([subQ0]),TDD([makeQuery(id+"F0.imprint","IMPRINT",EDGE,{"disambiguationData":[TD([[makeQuery(id+"F0.imprint","INTERSECT",VERTEX,{"disambiguationData":[OD(0.0)],"derivedFrom":[subQ0,sQuery(id+"F0.wireOp",EDGE,"E16.1.0")]}),1.0]])],"derivedFrom":subQ0})])],"isStart":true});}
            fillet(context, id + "F3", {"entities" : qUnion([Q0, Q1, Q2, Q3, Q4, Q5, Q6, Q7, Q8, Q9, Q10, Q11, Q12, Q13, Q14, Q15, Q16, Q17, Q18, Q19, Q20, Q21, Q22, Q23, Q24, Q25, Q26, Q27, Q28, Q29, Q30, Q31, Q32, Q33, Q34, Q35, Q36, Q37, Q38, Q39, Q40]), "radius" : 2 * mm, "tangentPropagation" : true, "allowEdgeOverflow" : false});
        }
    });
